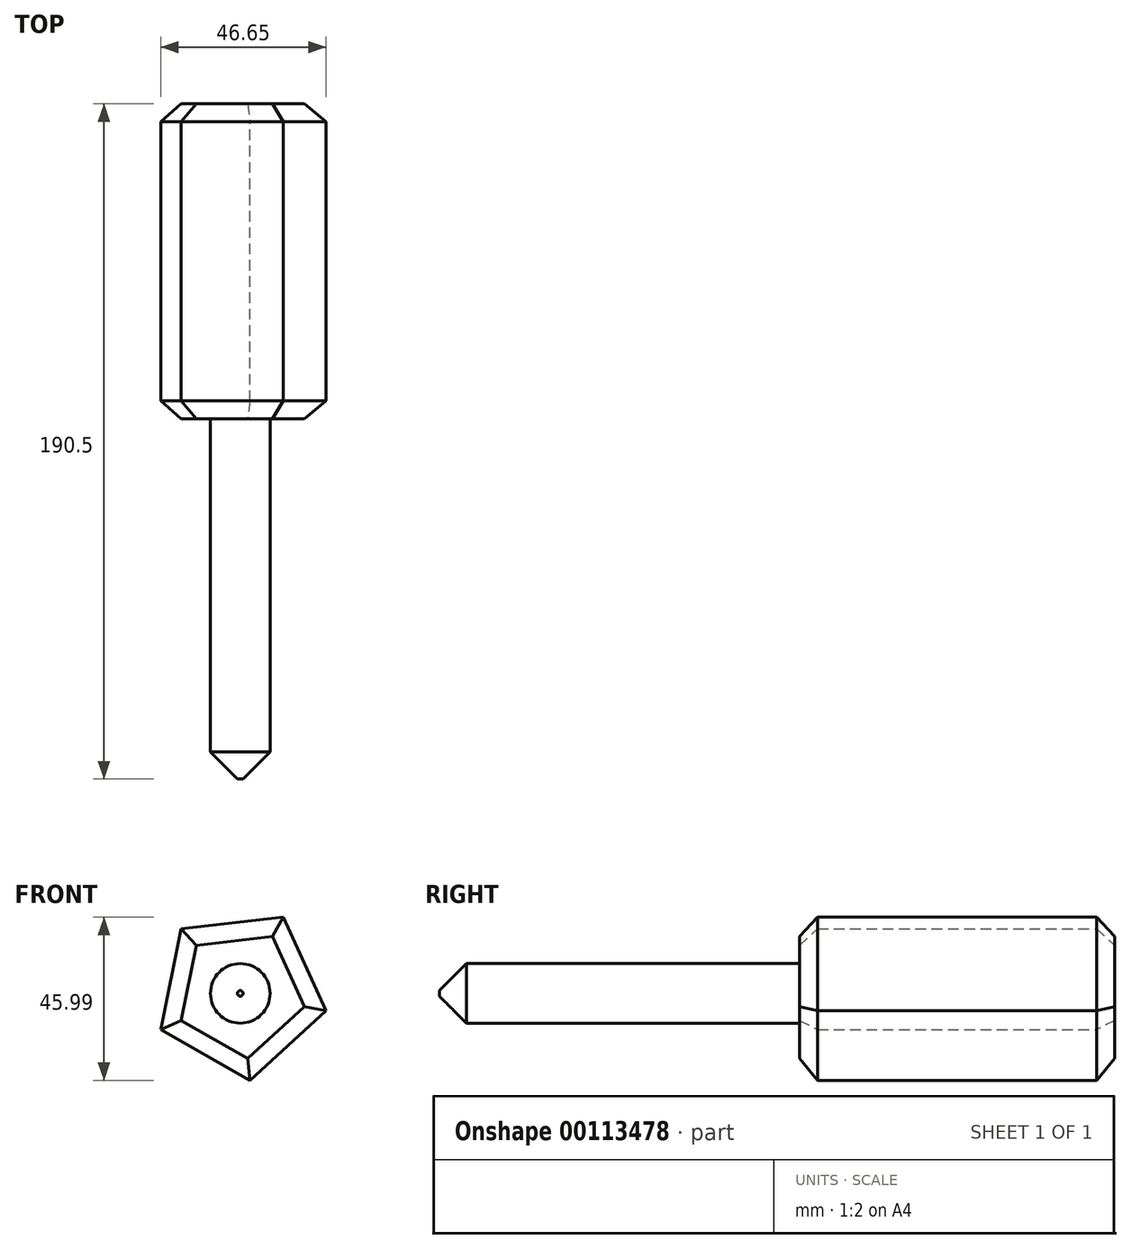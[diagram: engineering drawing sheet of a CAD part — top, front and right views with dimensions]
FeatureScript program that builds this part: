
annotation { "Feature Type Name" : "Feature", "Feature Type Description" : "" }
export const myFeature = defineFeature(function(context is Context, id is Id, definition is map)
    precondition{}
    {
        {
            var Q0;
            Q0=qCreatedBy(makeId("Front.planeOp"),FACE);
            var sketch = newSketch(context, id + "F0", { "sketchPlane" : qUnion([Q0])});
            skCircle(sketch, "E0.cCircle", {"center": v(0, 0) * mm, "radius": 19.97 * mm, "construction": true});
            skLineSegment(sketch, "E0.0", {"start": v(2.77, -24.52) * mm, "end": v(-22.47, -10.22) * mm});
            skLineSegment(sketch, "E0.1", {"start": v(-22.47, -10.22) * mm, "end": v(-16.66, 18.21) * mm});
            skLineSegment(sketch, "E0.2", {"start": v(-16.66, 18.21) * mm, "end": v(12.17, 21.47) * mm});
            skLineSegment(sketch, "E0.3", {"start": v(12.17, 21.47) * mm, "end": v(24.18, -4.94) * mm});
            skLineSegment(sketch, "E0.4", {"start": v(24.18, -4.94) * mm, "end": v(2.77, -24.52) * mm});
            skPoint(sketch, "E0.0.midPoint", {"position": v(-9.85, -17.37) * mm});
            skSolve(sketch);
        }
        {
            var Q0;
            Q0 = qSketchRegion(id + "F0", true);
            extrude(context, id + "F1", {"entities" : qUnion([Q0]), "depth" : 88.9 * mm});
        }
        {
            var Q0;
            Q0=makeQuery(id+"F1.opExtrude","CAP_EDGE",EDGE,{"disambiguationData":[OSD([sQuery(id+"F0.wireOp",EDGE,"E0.0")])],"isStart":false});
            chamfer(context, id + "F2", {"entities" : qUnion([Q0]), "width" : 5.08 * mm, "tangentPropagation" : true});
        }
        {
            var Q0;
            Q0=makeQuery(id+"F1.opExtrude","CAP_EDGE",EDGE,{"disambiguationData":[OSD([sQuery(id+"F0.wireOp",EDGE,"E0.1")])],"isStart":false});
            chamfer(context, id + "F3", {"entities" : qUnion([Q0]), "width" : 5.08 * mm, "tangentPropagation" : true});
        }
        {
            var Q0;
            Q0=makeQuery(id+"F1.opExtrude","CAP_EDGE",EDGE,{"disambiguationData":[OSD([sQuery(id+"F0.wireOp",EDGE,"E0.2")])],"isStart":false});
            chamfer(context, id + "F4", {"entities" : qUnion([Q0]), "width" : 5.08 * mm, "tangentPropagation" : true});
        }
        {
            var Q0;
            Q0=makeQuery(id+"F1.opExtrude","CAP_EDGE",EDGE,{"disambiguationData":[OSD([sQuery(id+"F0.wireOp",EDGE,"E0.3")])],"isStart":false});
            chamfer(context, id + "F5", {"entities" : qUnion([Q0]), "width" : 5.08 * mm, "tangentPropagation" : true});
        }
        {
            var Q0;
            Q0=makeQuery(id+"F1.opExtrude","CAP_EDGE",EDGE,{"disambiguationData":[OSD([sQuery(id+"F0.wireOp",EDGE,"E0.4")])],"isStart":false});
            chamfer(context, id + "F6", {"entities" : qUnion([Q0]), "width" : 5.08 * mm, "tangentPropagation" : true});
        }
        {
            var Q0;
            Q0=makeQuery(id+"F1.opExtrude","CAP_EDGE",EDGE,{"disambiguationData":[OSD([sQuery(id+"F0.wireOp",EDGE,"E0.1")])],"isStart":true});
            var Q1;
            Q1=makeQuery(id+"F1.opExtrude","CAP_EDGE",EDGE,{"disambiguationData":[OSD([sQuery(id+"F0.wireOp",EDGE,"E0.2")])],"isStart":true});
            var Q2;
            Q2=makeQuery(id+"F1.opExtrude","CAP_EDGE",EDGE,{"disambiguationData":[OSD([sQuery(id+"F0.wireOp",EDGE,"E0.3")])],"isStart":true});
            var Q3;
            Q3=makeQuery(id+"F1.opExtrude","CAP_EDGE",EDGE,{"disambiguationData":[OSD([sQuery(id+"F0.wireOp",EDGE,"E0.4")])],"isStart":true});
            var Q4;
            Q4=makeQuery(id+"F1.opExtrude","CAP_EDGE",EDGE,{"disambiguationData":[OSD([sQuery(id+"F0.wireOp",EDGE,"E0.0")])],"isStart":true});
            chamfer(context, id + "F7", {"entities" : qUnion([Q0, Q1, Q2, Q3, Q4]), "width" : 5.08 * mm, "tangentPropagation" : true});
        }
        {
            var Q0;
            Q0=makeQuery(id+"F1.opExtrude","CAP_FACE",FACE,{"disambiguationData":[OSD([sQuery(id+"F0.wireOp",EDGE,"E0.0"),sQuery(id+"F0.wireOp",EDGE,"E0.1"),sQuery(id+"F0.wireOp",EDGE,"E0.2"),sQuery(id+"F0.wireOp",EDGE,"E0.3"),sQuery(id+"F0.wireOp",EDGE,"E0.4")])],"isStart":false});
            var sketch = newSketch(context, id + "F8", { "sketchPlane" : qUnion([Q0])});
            skCircle(sketch, "E1", {"center": v(0, 0) * mm, "radius": 8.41 * mm});
            skSolve(sketch);
        }
        {
            var Q0;
            Q0 = qSketchRegion(id + "F8", true);
            extrude(context, id + "F9", {"entities" : qUnion([Q0]), "operationType" : NewBodyOperationType.ADD, "depth" : 101.6 * mm});
        }
        {
            var Q0;
            Q0=makeQuery(id+"F9.opExtrude","CAP_EDGE",EDGE,{"disambiguationData":[OSD([sQuery(id+"F8.wireOp",EDGE,"E1")])],"isStart":false});
            chamfer(context, id + "F10", {"entities" : qUnion([Q0]), "width" : 7.62 * mm, "tangentPropagation" : true});
        }
    });
